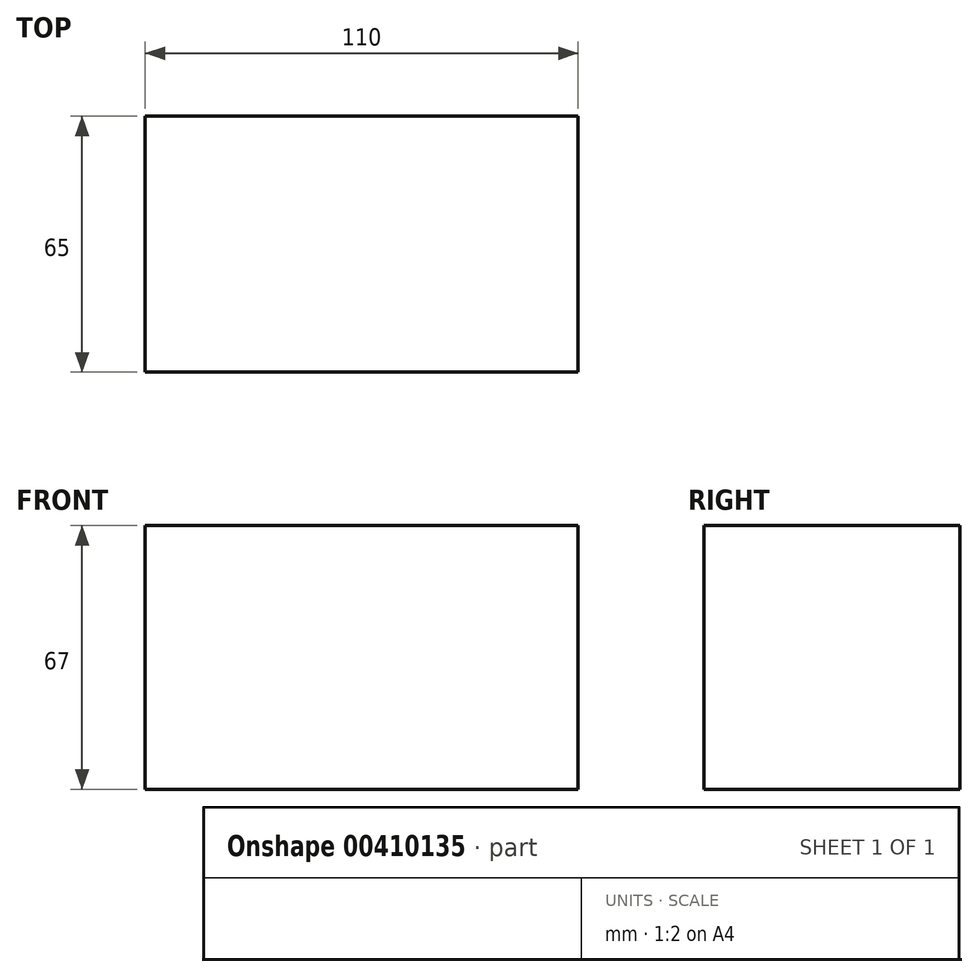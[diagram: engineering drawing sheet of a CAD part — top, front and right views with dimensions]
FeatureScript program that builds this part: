
annotation { "Feature Type Name" : "Feature", "Feature Type Description" : "" }
export const myFeature = defineFeature(function(context is Context, id is Id, definition is map)
    precondition{}
    {
        {
            var Q0;
            Q0=qCreatedBy(makeId("Top.planeOp"),FACE);
            var sketch = newSketch(context, id + "F0", { "sketchPlane" : qUnion([Q0])});
            skLineSegment(sketch, "E0.bottom", {"start": v(0, 0) * mm, "end": v(110, 0) * mm});
            skLineSegment(sketch, "E0.top", {"start": v(0, 65) * mm, "end": v(110, 65) * mm});
            skLineSegment(sketch, "E0.left", {"start": v(0, 0) * mm, "end": v(0, 65) * mm});
            skLineSegment(sketch, "E0.right", {"start": v(110, 0) * mm, "end": v(110, 65) * mm});
            skSolve(sketch);
        }
        {
            var Q0;
            Q0=qSketchRegion(id+"F0",true);
            extrude(context, id + "F1", {"entities" : qUnion([Q0]), "depth" : 67 * mm});
        }
    });
